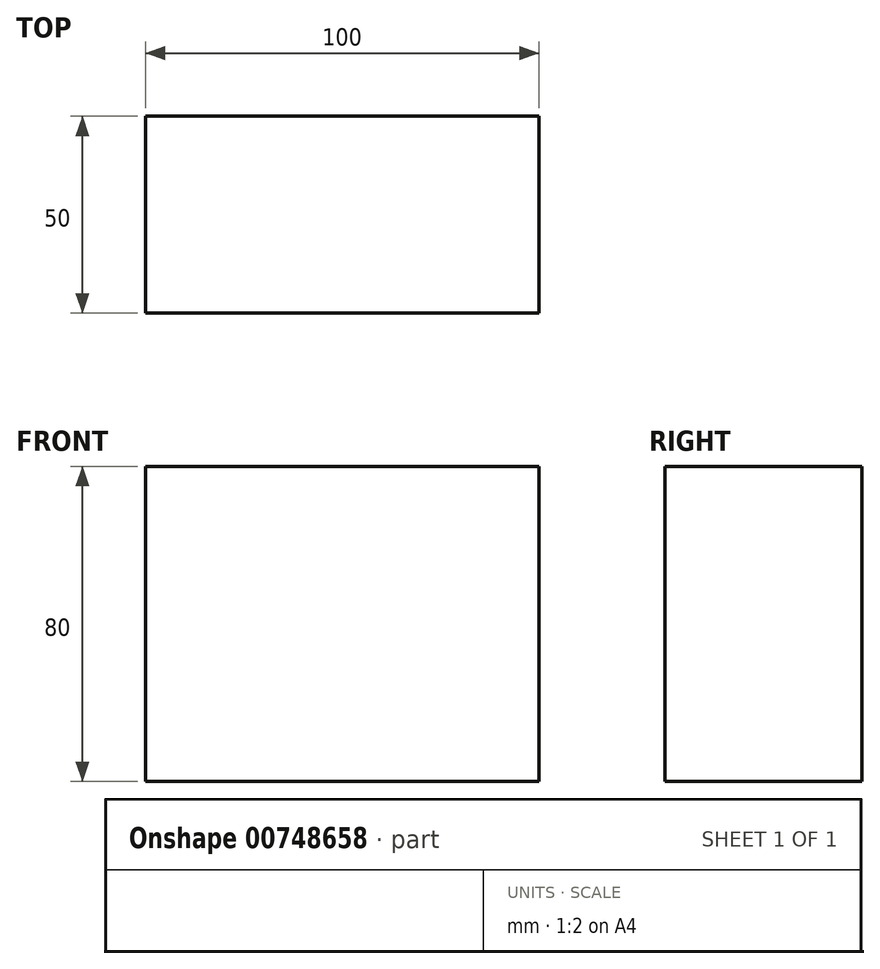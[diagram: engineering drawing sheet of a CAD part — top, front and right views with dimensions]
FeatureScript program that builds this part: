
annotation { "Feature Type Name" : "Feature", "Feature Type Description" : "" }
export const myFeature = defineFeature(function(context is Context, id is Id, definition is map)
    precondition{}
    {
        {
            var Q0;
            Q0=qCreatedBy(makeId("Top.planeOp"),FACE);
            var sketch = newSketch(context, id + "F0", { "sketchPlane" : qUnion([Q0])});
            skLineSegment(sketch, "E0", {"start": v(-50, 25) * mm, "end": v(50, 25) * mm});
            skLineSegment(sketch, "E1", {"start": v(50, 25) * mm, "end": v(50, -25) * mm});
            skLineSegment(sketch, "E2", {"start": v(50, -25) * mm, "end": v(-50, -25) * mm});
            skLineSegment(sketch, "E3", {"start": v(-50, -25) * mm, "end": v(-50, 25) * mm});
            skLineSegment(sketch, "E4", {"start": v(-50, -25) * mm, "end": v(50, 25) * mm});
            skSolve(sketch);
        }
        {
            var Q0;
            Q0 = qSketchRegion(id + "F0", true);
            extrude(context, id + "F1", {"entities" : qUnion([Q0]), "depth" : 80 * mm, "offsetDistance" : 25 * mm});
        }
    });
